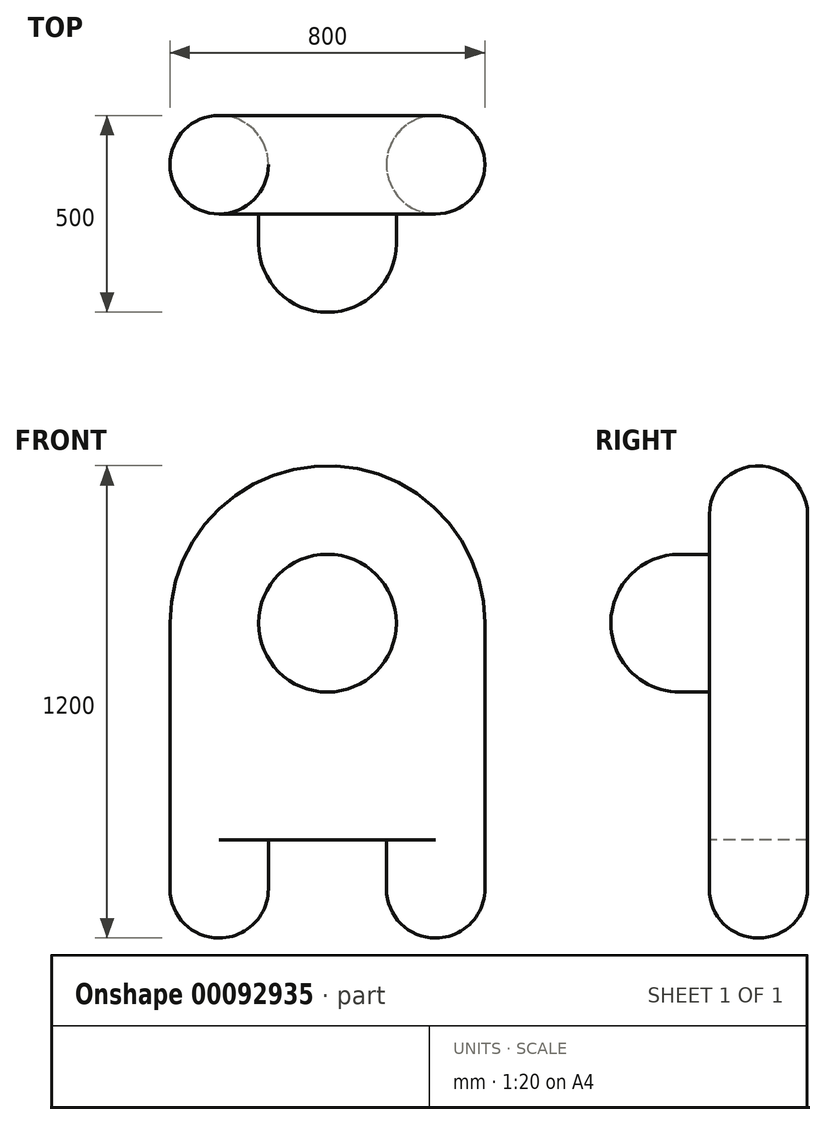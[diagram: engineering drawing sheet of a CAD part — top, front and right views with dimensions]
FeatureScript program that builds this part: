
annotation { "Feature Type Name" : "Feature", "Feature Type Description" : "" }
export const myFeature = defineFeature(function(context is Context, id is Id, definition is map)
    precondition{}
    {
        {
            var Q0;
            Q0=qCreatedBy(makeId("Front.planeOp"),FACE);
            var sketch = newSketch(context, id + "F0", { "sketchPlane" : qUnion([Q0])});
            skArc(sketch, "E0", {"start": v(400, 0) * mm, "mid": v(0, 400) * mm, "end": v(-400, 0) * mm});
            skLineSegment(sketch, "E1.top", {"start": v(400, -800) * mm, "end": v(150, -800) * mm});
            skLineSegment(sketch, "E1.left", {"start": v(400, 0) * mm, "end": v(400, -800) * mm});
            skLineSegment(sketch, "E1.right", {"start": v(-400, 0) * mm, "end": v(-400, -800) * mm});
            skPoint(sketch, "E1.bottom.end.orphan", {"position": v(-400, 800) * mm});
            skPoint(sketch, "E2.orphan", {"position": v(400, 800) * mm});
            skLineSegment(sketch, "E3.bottom", {"start": v(-150, -550) * mm, "end": v(150, -550) * mm});
            skLineSegment(sketch, "E3.left", {"start": v(-150, -550) * mm, "end": v(-150, -800) * mm});
            skLineSegment(sketch, "E3.right", {"start": v(150, -550) * mm, "end": v(150, -800) * mm});
            skPoint(sketch, "E3.middle", {"position": v(0, -800) * mm});
            skPoint(sketch, "E3.top.end.orphan", {"position": v(150, -1050) * mm});
            skPoint(sketch, "E3.top.start.orphan", {"position": v(-150, -1050) * mm});
            skLineSegment(sketch, "E4.trimOffspring", {"start": v(-150, -800) * mm, "end": v(-400, -800) * mm});
            skSolve(sketch);
        }
        {
            var Q0;
            Q0 = qSketchRegion(id + "F0", true);
            extrude(context, id + "F1", {"entities" : qUnion([Q0]), "endBound" : BoundingType.SYMMETRIC, "depth" : 250 * mm});
        }
        {
            var Q0;
            Q0=makeQuery(id+"F1.opExtrude","CAP_FACE",FACE,{"disambiguationData":[OSD([sQuery(id+"F0.wireOp",EDGE,"E0"),sQuery(id+"F0.wireOp",EDGE,"E1.top"),sQuery(id+"F0.wireOp",EDGE,"E1.left"),sQuery(id+"F0.wireOp",EDGE,"E1.right"),sQuery(id+"F0.wireOp",EDGE,"E3.bottom"),sQuery(id+"F0.wireOp",EDGE,"E3.left"),sQuery(id+"F0.wireOp",EDGE,"E3.right"),sQuery(id+"F0.wireOp",EDGE,"E4.trimOffspring")])],"isStart":false});
            var sketch = newSketch(context, id + "F2", { "sketchPlane" : qUnion([Q0])});
            skCircle(sketch, "E5", {"center": v(0, 0) * mm, "radius": 175 * mm});
            skSolve(sketch);
        }
        {
            var Q0;
            Q0 = qSketchRegion(id + "F2", true);
            extrude(context, id + "F3", {"entities" : qUnion([Q0]), "operationType" : NewBodyOperationType.ADD, "endBound" : BoundingType.SYMMETRIC, "depth" : 500 * mm});
        }
        {
            var Q0;
            Q0=makeQuery(id+"F1.opExtrude","SWEPT_FACE",FACE,{"disambiguationData":[OSD([sQuery(id+"F0.wireOp",EDGE,"E4.trimOffspring")])]});
            var Q1;
            Q1=makeQuery(id+"F1.opExtrude","SWEPT_FACE",FACE,{"disambiguationData":[OSD([sQuery(id+"F0.wireOp",EDGE,"E1.top")])]});
            fillet(context, id + "F4", {"entities" : qUnion([Q0, Q1]), "radius" : 125 * mm, "tangentPropagation" : true, "allowEdgeOverflow" : false});
        }
        {
            var Q0;
            Q0=makeQuery(id+"F1.opExtrude","CAP_EDGE",EDGE,{"disambiguationData":[OSD([sQuery(id+"F0.wireOp",EDGE,"E1.left")])],"isStart":false});
            var Q1;
            Q1=makeQuery(id+"F1.opExtrude","CAP_EDGE",EDGE,{"disambiguationData":[OSD([sQuery(id+"F0.wireOp",EDGE,"E1.left")])],"isStart":true});
            var Q2;
            Q2=makeQuery(id+"F1.opExtrude","CAP_EDGE",EDGE,{"disambiguationData":[OSD([sQuery(id+"F0.wireOp",EDGE,"E1.right")])],"isStart":false});
            var Q3;
            Q3=makeQuery(id+"F1.opExtrude","CAP_EDGE",EDGE,{"disambiguationData":[OSD([sQuery(id+"F0.wireOp",EDGE,"E1.right")])],"isStart":true});
            var Q4;
            Q4=makeQuery(id+"F1.opExtrude","CAP_EDGE",EDGE,{"disambiguationData":[OSD([sQuery(id+"F0.wireOp",EDGE,"E3.left")])],"isStart":true});
            var Q5;
            Q5=makeQuery(id+"F1.opExtrude","CAP_EDGE",EDGE,{"disambiguationData":[OSD([sQuery(id+"F0.wireOp",EDGE,"E3.left")])],"isStart":false});
            var Q6;
            Q6=makeQuery(id+"F1.opExtrude","CAP_EDGE",EDGE,{"disambiguationData":[OSD([sQuery(id+"F0.wireOp",EDGE,"E3.right")])],"isStart":false});
            var Q7;
            Q7=makeQuery(id+"F1.opExtrude","CAP_EDGE",EDGE,{"disambiguationData":[OSD([sQuery(id+"F0.wireOp",EDGE,"E3.right")])],"isStart":true});
            fillet(context, id + "F5", {"entities" : qUnion([Q0, Q1, Q2, Q3, Q4, Q5, Q6, Q7]), "radius" : 125 * mm, "tangentPropagation" : true, "allowEdgeOverflow" : false});
        }
        {
            var Q0;
            Q0=makeQuery(id+"F3.opExtrude","CAP_FACE",FACE,{"disambiguationData":[OSD([sQuery(id+"F2.wireOp",EDGE,"E5")])],"isStart":false});
            fillet(context, id + "F6", {"entities" : qUnion([Q0]), "radius" : 175 * mm, "tangentPropagation" : true, "allowEdgeOverflow" : false});
        }
    });
